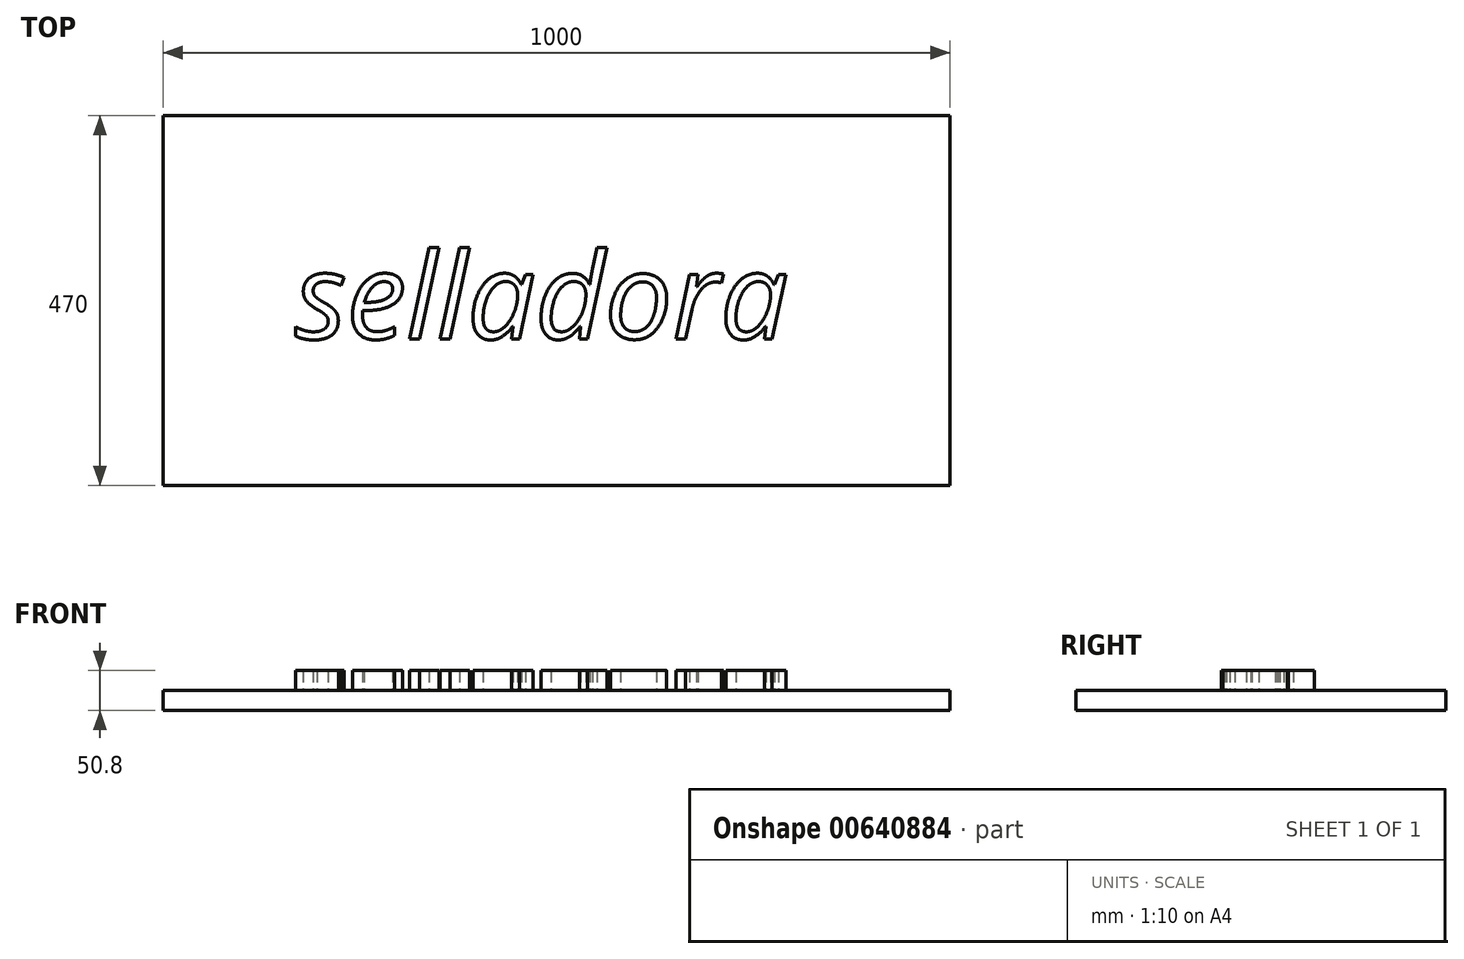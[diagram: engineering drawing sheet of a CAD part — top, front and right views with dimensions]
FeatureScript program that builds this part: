
annotation { "Feature Type Name" : "Feature", "Feature Type Description" : "" }
export const myFeature = defineFeature(function(context is Context, id is Id, definition is map)
    precondition{}
    {
        {
            var Q0;
            Q0=qCreatedBy(makeId("Top.planeOp"),FACE);
            var sketch = newSketch(context, id + "F0", { "sketchPlane" : qUnion([Q0])});
            skLineSegment(sketch, "E0.bottom", {"start": v(-489.06, 351.45) * mm, "end": v(510.94, 351.45) * mm});
            skLineSegment(sketch, "E0.top", {"start": v(-489.06, -118.55) * mm, "end": v(510.94, -118.55) * mm});
            skLineSegment(sketch, "E0.left", {"start": v(-489.06, 351.45) * mm, "end": v(-489.06, -118.55) * mm});
            skLineSegment(sketch, "E0.right", {"start": v(510.94, 351.45) * mm, "end": v(510.94, -118.55) * mm});
            skSolve(sketch);
        }
        {
            var Q0;
            Q0 = qSketchRegion(id + "F0", true);
            extrude(context, id + "F1", {"entities" : qUnion([Q0]), "depth" : 25.4 * mm, "offsetDistance" : 25.4 * mm});
        }
        {
            var Q0;
            Q0=makeQuery(id+"F1.opExtrude","CAP_FACE",FACE,{"disambiguationData":[OSD([sQuery(id+"F0.wireOp",EDGE,"E0.bottom"),sQuery(id+"F0.wireOp",EDGE,"E0.top"),sQuery(id+"F0.wireOp",EDGE,"E0.left"),sQuery(id+"F0.wireOp",EDGE,"E0.right")])],"isStart":false});
            var sketch = newSketch(context, id + "F2", { "sketchPlane" : qUnion([Q0])});
            skText(sketch, "E1", { "text": "selladora ", "fontName": "OpenSans-Italic.ttf"});
            const initialGuessF2  = {"E1": [-0.32107, 0.0677, 1, 0, 0.11014]};
            skSetInitialGuess(sketch, initialGuessF2);
            skSolve(sketch);
        }
        {
            var Q0;
            Q0 = qSketchRegion(id + "F2", true);
            extrude(context, id + "F3", {"entities" : qUnion([Q0]), "operationType" : NewBodyOperationType.ADD, "depth" : 25.4 * mm, "offsetDistance" : 25.4 * mm});
        }
    });
